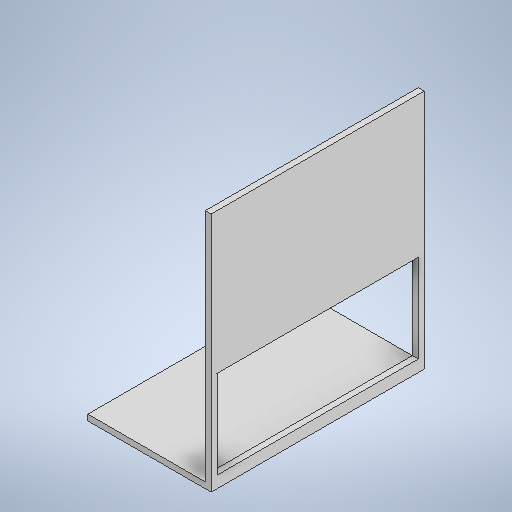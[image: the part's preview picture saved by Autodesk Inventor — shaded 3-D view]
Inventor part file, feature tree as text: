
AUTODESK INVENTOR PART (.ipt)
format: ipt  version: 2025.1 (Build 291241020, 241B)  size: 231,936 bytes
history: native  units: in
note: dims shown in document units (in); Inventor stores cm internally (conversion verified against a paired STEP export)
features: extrude x3, sketch x3
ambient origin geometry x8: Origin, YZ Plane, XZ Plane, XY Plane, X Axis, Y Axis, Z Axis, Center Point
bodies: Solid1 (feature_tree)
feature tree (6):
  extrude  "Extrusion1"  Depth=4.2in
  extrude  "Extrusion2"  Depth=0.2in
  extrude  "Extrusion3"  Depth=0.2in
  sketch  "Sketch1"  dims[d0=7.25in d1=4.2in]
  sketch  "Sketch2"  dims[d2=0.2in d3=0.0in d4=0.2in]
  sketch  "Sketch3"  dims[d5=8.0in d6=0.0in d7=0.2in d8=0.2in d9=0.4in d10=3.0in d11=8.0in d12=0.0in]
